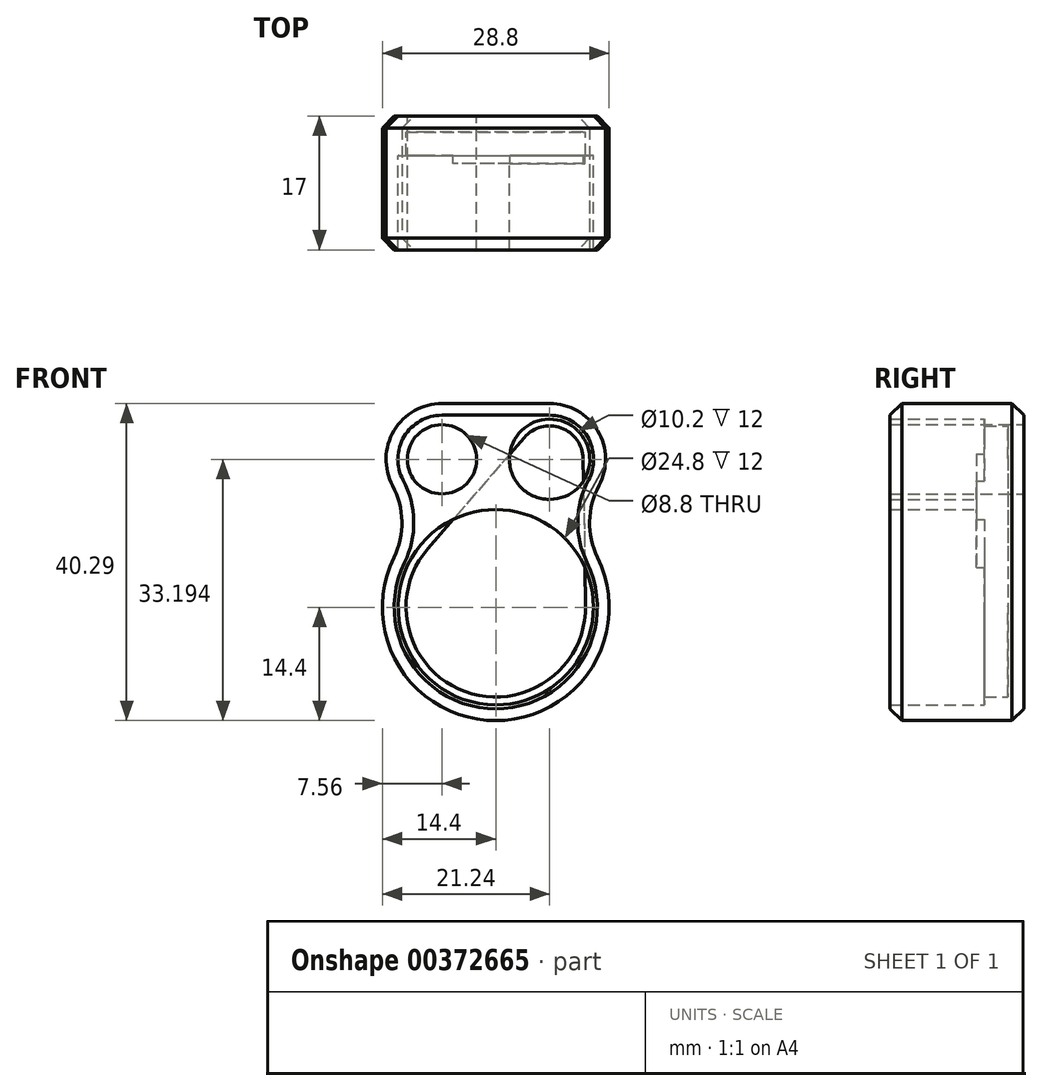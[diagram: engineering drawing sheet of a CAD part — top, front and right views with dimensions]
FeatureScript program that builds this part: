
annotation { "Feature Type Name" : "Feature", "Feature Type Description" : "" }
export const myFeature = defineFeature(function(context is Context, id is Id, definition is map)
    precondition{}
    {
        {
            var Q0;
            Q0=qCreatedBy(makeId("Front.planeOp"),FACE);
            var sketch = newSketch(context, id + "F0", { "sketchPlane" : qUnion([Q0])});
            skCircle(sketch, "E0", {"center": v(0, 0) * mm, "radius": 12.4 * mm});
            skArc(sketch, "E1", {"start": v(8.21, 11.83) * mm, "mid": v(13.9, 19.48) * mm, "end": v(6.84, 25.9) * mm});
            skArc(sketch, "E2", {"start": v(-8.21, 11.83) * mm, "mid": v(0, -14.4) * mm, "end": v(8.21, 11.83) * mm});
            skArc(sketch, "E3", {"start": v(-8.61, 7.47) * mm, "mid": v(-3.9, -10.71) * mm, "end": v(11.4, 0.19) * mm});
            skCircle(sketch, "E4", {"center": v(6.84, 18.8) * mm, "radius": 4.25 * mm});
            skLineSegment(sketch, "E5", {"start": v(3.63, 21.58) * mm, "end": v(-8.61, 7.47) * mm});
            skLineSegment(sketch, "E6", {"start": v(11.09, 18.86) * mm, "end": v(11.4, 0.19) * mm});
            skCircle(sketch, "E7.converted", {"center": v(6.84, 18.8) * mm, "radius": 5.1 * mm});
            skLineSegment(sketch, "E8", {"start": v(0, 0) * mm, "end": v(6.84, 18.8) * mm, "construction": true});
            skLineSegment(sketch, "E9", {"start": v(0, 0) * mm, "end": v(0, -14.4) * mm, "construction": true});
            skCircle(sketch, "E10", {"center": v(-6.84, 18.8) * mm, "radius": 4.4 * mm});
            skLineSegment(sketch, "E11", {"start": v(-6.84, 18.8) * mm, "end": v(0, 0) * mm, "construction": true});
            skArc(sketch, "E12.trimOffspring", {"start": v(-6.84, 25.9) * mm, "mid": v(-13.9, 19.48) * mm, "end": v(-8.21, 11.83) * mm});
            skLineSegment(sketch, "E13", {"start": v(-6.84, 25.9) * mm, "end": v(6.84, 25.9) * mm});
            skSolve(sketch);
        }
        {
            var Q0;
            Q0=makeQuery(id+"F0.imprint","IMPRINT",FACE,{"disambiguationData":[TD([[makeQuery(id+"F0.imprint","IMPRINT",EDGE,{"derivedFrom":sQuery(id+"F0.wireOp",EDGE,"E1")}),1.0]])]});
            var Q1;
            {var subQ0=sQuery(id+"F0.wireOp",EDGE,"E5");var subQ1=sQuery(id+"F0.wireOp",EDGE,"E0");var subQ2=makeQuery(id+"F0.imprint","INTERSECT",VERTEX,{"derivedFrom":[subQ1,subQ0]});Q1=makeQuery(id+"F0.imprint","IMPRINT",FACE,{"disambiguationData":[TD([[makeQuery(id+"F0.imprint","IMPRINT",EDGE,{"disambiguationData":[TD([[subQ2,1.0]])],"derivedFrom":subQ1}),-1.0]])]});}
            var Q2;
            {var subQ0=sQuery(id+"F0.wireOp",EDGE,"E6");var subQ1=sQuery(id+"F0.wireOp",EDGE,"E1");var subQ2=makeQuery(id+"F0.imprint","INTERSECT",VERTEX,{"derivedFrom":[subQ1,subQ0]});Q2=makeQuery(id+"F0.imprint","IMPRINT",FACE,{"disambiguationData":[TD([[makeQuery(id+"F0.imprint","IMPRINT",EDGE,{"disambiguationData":[TD([[subQ2,-1.0]])],"derivedFrom":subQ1}),1.0]])]});}
            var Q3;
            {var subQ0=sQuery(id+"F0.wireOp",EDGE,"E5");var subQ1=sQuery(id+"F0.wireOp",EDGE,"E0");var subQ2=makeQuery(id+"F0.imprint","INTERSECT",VERTEX,{"derivedFrom":[subQ1,subQ0]});Q3=makeQuery(id+"F0.imprint","IMPRINT",FACE,{"disambiguationData":[TD([[makeQuery(id+"F0.imprint","IMPRINT",EDGE,{"disambiguationData":[TD([[subQ2,-1.0]])],"derivedFrom":subQ1}),-1.0]])]});}
            extrude(context, id + "F1", {"entities" : qUnion([Q0, Q1, Q2, Q3]), "depth" : 5 * mm, "offsetDistance" : 25 * mm});
        }
        {
            var Q0;
            {var subQ0=sQuery(id+"F0.wireOp",EDGE,"E6");var subQ1=sQuery(id+"F0.wireOp",EDGE,"E1");var subQ2=makeQuery(id+"F0.imprint","INTERSECT",VERTEX,{"derivedFrom":[subQ1,subQ0]});Q0=makeQuery(id+"F0.imprint","IMPRINT",FACE,{"disambiguationData":[TD([[makeQuery(id+"F0.imprint","IMPRINT",EDGE,{"disambiguationData":[TD([[subQ2,-1.0]])],"derivedFrom":subQ1}),1.0]])]});}
            var Q1;
            {var subQ3=sQuery(id+"F0.wireOp",EDGE,"E5");var subQ9=sQuery(id+"F0.wireOp",EDGE,"E0");var subQ10=makeQuery(id+"F0.imprint","INTERSECT",VERTEX,{"derivedFrom":[subQ9,subQ3]});Q1=makeQuery(id+"F0.imprint","IMPRINT",FACE,{"disambiguationData":[TD([[makeQuery(id+"F0.imprint","IMPRINT",EDGE,{"disambiguationData":[TD([[subQ10,1.0]])],"derivedFrom":subQ9}),-1.0]])]});}
            var Q2;
            {var subQ0=sQuery(id+"F0.wireOp",EDGE,"E5");var subQ1=sQuery(id+"F0.wireOp",EDGE,"E0");var subQ2=makeQuery(id+"F0.imprint","INTERSECT",VERTEX,{"derivedFrom":[subQ1,subQ0]});Q2=makeQuery(id+"F0.imprint","IMPRINT",FACE,{"disambiguationData":[TD([[makeQuery(id+"F0.imprint","IMPRINT",EDGE,{"disambiguationData":[TD([[subQ2,-1.0]])],"derivedFrom":subQ1}),-1.0]])]});}
            var Q3;
            {var subQ0=sQuery(id+"F0.wireOp",EDGE,"E4");var subQ1=makeQuery(id+"F0.imprint","INTERSECT",VERTEX,{"derivedFrom":[subQ0,sQuery(id+"F0.wireOp",EDGE,"E5")]});Q3=makeQuery(id+"F0.imprint","IMPRINT",FACE,{"disambiguationData":[TD([[makeQuery(id+"F0.imprint","IMPRINT",EDGE,{"disambiguationData":[TD([[subQ1,1.0]])],"derivedFrom":subQ0}),1.0]])]});}
            var Q4;
            {var subQ0=sQuery(id+"F0.wireOp",EDGE,"E5");var subQ1=sQuery(id+"F0.wireOp",EDGE,"E4");var subQ2=makeQuery(id+"F0.imprint","INTERSECT",VERTEX,{"derivedFrom":[subQ1,subQ0]});Q4=makeQuery(id+"F0.imprint","IMPRINT",FACE,{"disambiguationData":[TD([[makeQuery(id+"F0.imprint","IMPRINT",EDGE,{"disambiguationData":[TD([[subQ2,-1.0]])],"derivedFrom":subQ1}),-1.0]])]});}
            var Q5;
            {var subQ0=sQuery(id+"F0.wireOp",EDGE,"E5");var subQ1=sQuery(id+"F0.wireOp",EDGE,"E4");var subQ2=makeQuery(id+"F0.imprint","INTERSECT",VERTEX,{"derivedFrom":[subQ1,subQ0]});Q5=makeQuery(id+"F0.imprint","IMPRINT",FACE,{"disambiguationData":[TD([[makeQuery(id+"F0.imprint","IMPRINT",EDGE,{"disambiguationData":[TD([[subQ2,1.0]])],"derivedFrom":subQ1}),-1.0]])]});}
            var Q6;
            {var subQ5=sQuery(id+"F0.wireOp",EDGE,"E3");Q6=makeQuery(id+"F0.imprint","IMPRINT",FACE,{"disambiguationData":[TD([[makeQuery(id+"F0.imprint","IMPRINT",EDGE,{"derivedFrom":subQ5}),1.0]])]});}
            var Q7;
            {var subQ5=sQuery(id+"F0.wireOp",EDGE,"E3");Q7=makeQuery(id+"F0.imprint","IMPRINT",FACE,{"disambiguationData":[TD([[makeQuery(id+"F0.imprint","IMPRINT",EDGE,{"derivedFrom":subQ5}),-1.0]])]});}
            extrude(context, id + "F2", {"entities" : qUnion([Q0, Q1, Q2, Q3, Q4, Q5, Q6, Q7]), "operationType" : NewBodyOperationType.ADD, "oppositeDirection" : true, "depth" : 2 * mm, "offsetDistance" : 25 * mm});
        }
        {
            var Q0;
            {var subQ0=sQuery(id+"F0.wireOp",EDGE,"E2");var subQ1=sQuery(id+"F0.wireOp",EDGE,"E1");var subQ2=makeQuery(id+"F0.imprint","INTERSECT",VERTEX,{"disambiguationData":[OD(1.0)],"derivedFrom":[subQ1,subQ0]});Q0=makeQuery(id+"F2.boolean.opBoolean","MERGE",EDGE,{"derivedFrom":[makeQuery(id+"F1.opExtrude","SWEPT_EDGE",EDGE,{"disambiguationData":[OSD([subQ1,subQ0]),TDD([subQ2])]}),makeQuery(id+"F2.opExtrude","SWEPT_EDGE",EDGE,{"disambiguationData":[OSD([subQ1,subQ0]),TDD([subQ2])]})]});}
            var Q1;
            {var subQ0=sQuery(id+"F0.wireOp",EDGE,"E2");var subQ1=sQuery(id+"F0.wireOp",EDGE,"E1");var subQ2=makeQuery(id+"F0.imprint","INTERSECT",VERTEX,{"disambiguationData":[OD(0.0)],"derivedFrom":[subQ1,subQ0]});Q1=makeQuery(id+"F2.boolean.opBoolean","MERGE",EDGE,{"derivedFrom":[makeQuery(id+"F1.opExtrude","SWEPT_EDGE",EDGE,{"disambiguationData":[OSD([subQ1,subQ0]),TDD([subQ2])]}),makeQuery(id+"F2.opExtrude","SWEPT_EDGE",EDGE,{"disambiguationData":[OSD([subQ1,subQ0]),TDD([subQ2])]})]});}
            var Q2;
            {var subQ0=sQuery(id+"F0.wireOp",EDGE,"E12.trimOffspring");var subQ1=sQuery(id+"F0.wireOp",EDGE,"E2");Q2=makeQuery(id+"F2.boolean.opBoolean","MERGE",EDGE,{"derivedFrom":[makeQuery(id+"F1.opExtrude","SWEPT_EDGE",EDGE,{"disambiguationData":[OSD([subQ1,subQ0])]}),makeQuery(id+"F2.opExtrude","SWEPT_EDGE",EDGE,{"disambiguationData":[OSD([subQ1,subQ0])]})]});}
            fillet(context, id + "F3", {"entities" : qUnion([Q0, Q1, Q2]), "radius" : 10 * mm, "tangentPropagation" : true, "allowEdgeOverflow" : false});
        }
        {
            var Q0;
            {var subQ5=sQuery(id+"F0.wireOp",EDGE,"E3");Q0=makeQuery(id+"F0.imprint","IMPRINT",FACE,{"disambiguationData":[TD([[makeQuery(id+"F0.imprint","IMPRINT",EDGE,{"derivedFrom":subQ5}),-1.0]])]});}
            var Q1;
            {var subQ0=sQuery(id+"F0.wireOp",EDGE,"E5");var subQ1=sQuery(id+"F0.wireOp",EDGE,"E4");var subQ2=makeQuery(id+"F0.imprint","INTERSECT",VERTEX,{"derivedFrom":[subQ1,subQ0]});Q1=makeQuery(id+"F0.imprint","IMPRINT",FACE,{"disambiguationData":[TD([[makeQuery(id+"F0.imprint","IMPRINT",EDGE,{"disambiguationData":[TD([[subQ2,1.0]])],"derivedFrom":subQ1}),-1.0]])]});}
            extrude(context, id + "F4", {"entities" : qUnion([Q0, Q1]), "operationType" : NewBodyOperationType.ADD, "depth" : 3 * mm, "offsetDistance" : 25 * mm});
        }
        {
            var Q0;
            {var subQ5=sQuery(id+"F0.wireOp",EDGE,"E3");Q0=makeQuery(id+"F0.imprint","IMPRINT",FACE,{"disambiguationData":[TD([[makeQuery(id+"F0.imprint","IMPRINT",EDGE,{"derivedFrom":subQ5}),1.0]])]});}
            var Q1;
            {var subQ0=sQuery(id+"F0.wireOp",EDGE,"E5");var subQ1=sQuery(id+"F0.wireOp",EDGE,"E0");var subQ2=makeQuery(id+"F0.imprint","INTERSECT",VERTEX,{"derivedFrom":[subQ1,subQ0]});Q1=makeQuery(id+"F0.imprint","IMPRINT",FACE,{"disambiguationData":[TD([[makeQuery(id+"F0.imprint","IMPRINT",EDGE,{"disambiguationData":[TD([[subQ2,1.0]])],"derivedFrom":subQ1}),-1.0]])]});}
            var Q2;
            {var subQ0=sQuery(id+"F0.wireOp",EDGE,"E5");var subQ1=sQuery(id+"F0.wireOp",EDGE,"E4");var subQ2=makeQuery(id+"F0.imprint","INTERSECT",VERTEX,{"derivedFrom":[subQ1,subQ0]});Q2=makeQuery(id+"F0.imprint","IMPRINT",FACE,{"disambiguationData":[TD([[makeQuery(id+"F0.imprint","IMPRINT",EDGE,{"disambiguationData":[TD([[subQ2,-1.0]])],"derivedFrom":subQ1}),-1.0]])]});}
            var Q3;
            {var subQ0=sQuery(id+"F0.wireOp",EDGE,"E4");var subQ1=makeQuery(id+"F0.imprint","INTERSECT",VERTEX,{"derivedFrom":[subQ0,sQuery(id+"F0.wireOp",EDGE,"E5")]});Q3=makeQuery(id+"F0.imprint","IMPRINT",FACE,{"disambiguationData":[TD([[makeQuery(id+"F0.imprint","IMPRINT",EDGE,{"disambiguationData":[TD([[subQ1,1.0]])],"derivedFrom":subQ0}),1.0]])]});}
            var Q4;
            {var subQ0=sQuery(id+"F0.wireOp",EDGE,"E2");var subQ1=sQuery(id+"F0.wireOp",EDGE,"E1");var subQ2=makeQuery(id+"F0.imprint","INTERSECT",VERTEX,{"disambiguationData":[OD(1.0)],"derivedFrom":[subQ1,subQ0]});Q4=makeQuery(id+"F0.imprint","IMPRINT",FACE,{"disambiguationData":[TD([[makeQuery(id+"F0.imprint","IMPRINT",EDGE,{"disambiguationData":[TD([[subQ2,1.0]])],"derivedFrom":subQ1}),-1.0]])]});}
            var Q5;
            {var subQ0=sQuery(id+"F0.wireOp",EDGE,"E2");var subQ1=sQuery(id+"F0.wireOp",EDGE,"E1");var subQ2=makeQuery(id+"F0.imprint","INTERSECT",VERTEX,{"disambiguationData":[OD(0.0)],"derivedFrom":[subQ1,subQ0]});Q5=makeQuery(id+"F0.imprint","IMPRINT",FACE,{"disambiguationData":[TD([[makeQuery(id+"F0.imprint","IMPRINT",EDGE,{"disambiguationData":[TD([[subQ2,-1.0]])],"derivedFrom":subQ1}),-1.0]])]});}
            extrude(context, id + "F5", {"entities" : qUnion([Q0, Q1, Q2, Q3, Q4, Q5]), "operationType" : NewBodyOperationType.REMOVE, "depth" : 4 * mm, "offsetDistance" : 25 * mm});
        }
        {
            var Q0;
            Q0=makeQuery(id+"F1.opExtrude","CAP_FACE",FACE,{"disambiguationData":[OSD([sQuery(id+"F0.wireOp",EDGE,"E0"),sQuery(id+"F0.wireOp",EDGE,"E1"),sQuery(id+"F0.wireOp",EDGE,"E2"),sQuery(id+"F0.wireOp",EDGE,"E7.converted")])],"isStart":false});
            extrude(context, id + "F6", {"entities" : qUnion([Q0]), "operationType" : NewBodyOperationType.ADD, "depth" : 10 * mm, "offsetDistance" : 25 * mm});
        }
        {
            var Q0;
            Q0=makeQuery(id+"F2.opExtrude","CAP_EDGE",EDGE,{"disambiguationData":[OSD([sQuery(id+"F0.wireOp",EDGE,"E2")])],"isStart":false});
            var Q1;
            Q1=makeQuery(id+"F6.opExtrude","CAP_EDGE",EDGE,{"disambiguationData":[OSD([sQuery(id+"F0.wireOp",EDGE,"E2")])],"isStart":false});
            chamfer(context, id + "F7", {"entities" : qUnion([Q0, Q1]), "width" : 1.5 * mm, "tangentPropagation" : true});
        }
    });
